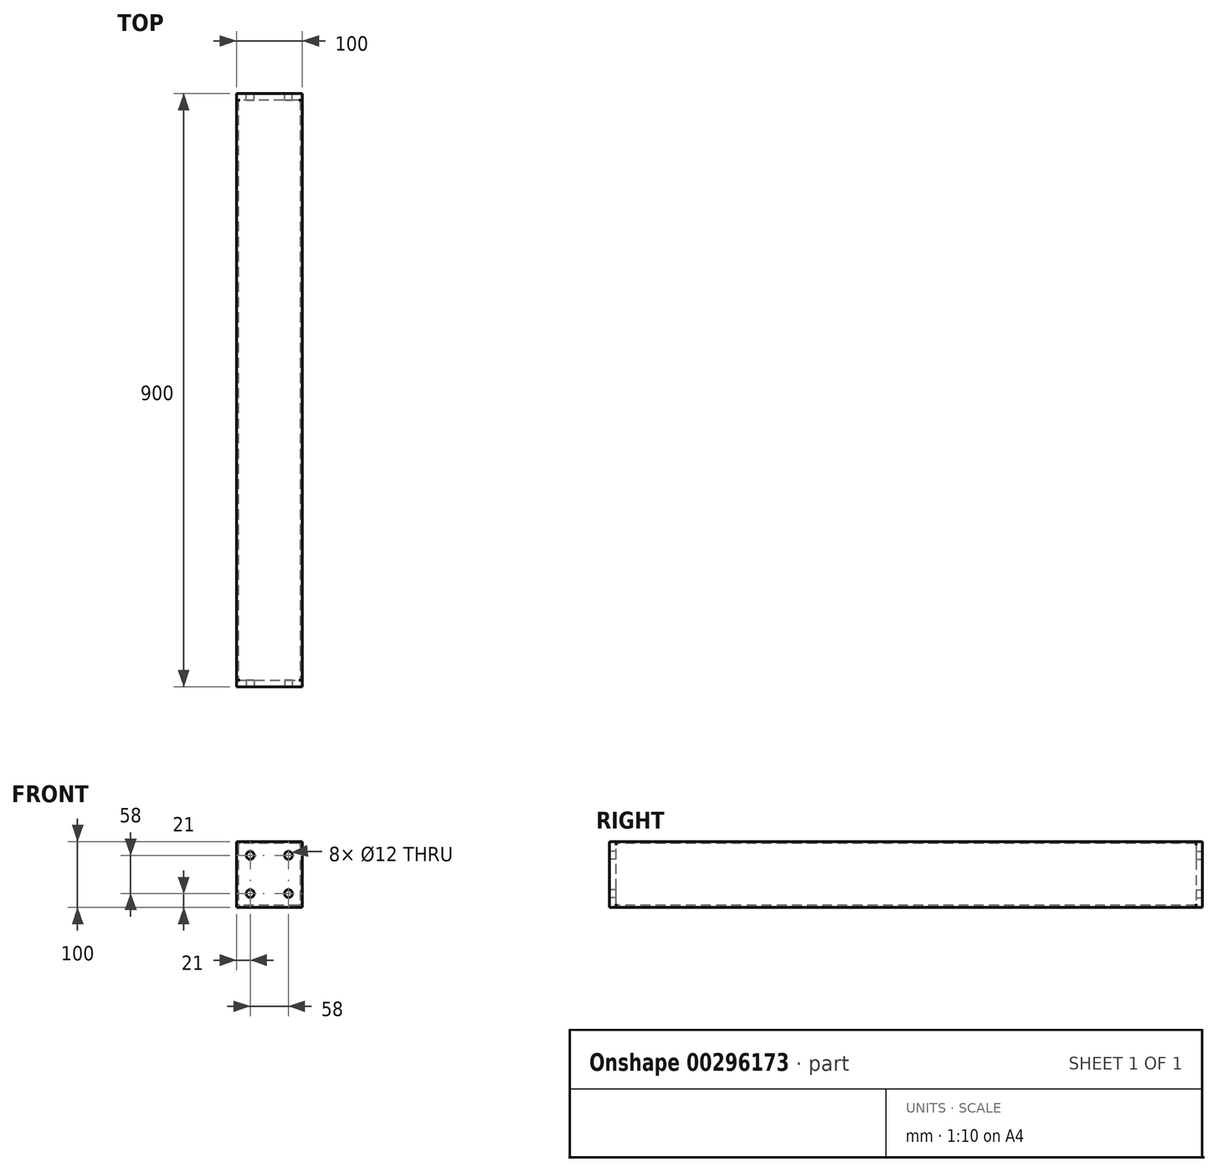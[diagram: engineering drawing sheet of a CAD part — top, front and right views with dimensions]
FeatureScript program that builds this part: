
annotation { "Feature Type Name" : "Feature", "Feature Type Description" : "" }
export const myFeature = defineFeature(function(context is Context, id is Id, definition is map)
    precondition{}
    {
        {
            var Q0;
            Q0=qCreatedBy(makeId("Front.planeOp"),FACE);
            var sketch = newSketch(context, id + "F0", { "sketchPlane" : qUnion([Q0])});
            skLineSegment(sketch, "E0.bottom", {"start": v(45, 50) * mm, "end": v(-45, 50) * mm});
            skLineSegment(sketch, "E0.top", {"start": v(45, -50) * mm, "end": v(-45, -50) * mm});
            skLineSegment(sketch, "E0.left", {"start": v(50, 45) * mm, "end": v(50, -45) * mm});
            skLineSegment(sketch, "E0.right", {"start": v(-50, 45) * mm, "end": v(-50, -45) * mm});
            skPoint(sketch, "E0.middle", {"position": v(0, 0) * mm});
            skPoint(sketch, "E1.visualSharp", {"position": v(-50, 50) * mm});
            skArc(sketch, "E1.filletArc", {"start": v(-45, 50) * mm, "mid": v(-48.54, 48.54) * mm, "end": v(-50, 45) * mm});
            skPoint(sketch, "E2.visualSharp", {"position": v(50, 50) * mm});
            skArc(sketch, "E2.filletArc", {"start": v(50, 45) * mm, "mid": v(48.54, 48.54) * mm, "end": v(45, 50) * mm});
            skPoint(sketch, "E3.visualSharp", {"position": v(50, -50) * mm});
            skArc(sketch, "E3.filletArc", {"start": v(45, -50) * mm, "mid": v(48.54, -48.54) * mm, "end": v(50, -45) * mm});
            skPoint(sketch, "E4.visualSharp", {"position": v(-50, -50) * mm});
            skArc(sketch, "E4.filletArc", {"start": v(-50, -45) * mm, "mid": v(-48.54, -48.54) * mm, "end": v(-45, -50) * mm});
            skArc(sketch, "E5.0", {"start": v(-45, 47) * mm, "mid": v(-46.41, 46.41) * mm, "end": v(-47, 45) * mm});
            skLineSegment(sketch, "E5.1", {"start": v(45, 47) * mm, "end": v(-45, 47) * mm});
            skLineSegment(sketch, "E5.2", {"start": v(-47, 45) * mm, "end": v(-47, -45) * mm});
            skArc(sketch, "E5.3", {"start": v(47, 45) * mm, "mid": v(46.41, 46.41) * mm, "end": v(45, 47) * mm});
            skArc(sketch, "E5.4", {"start": v(-47, -45) * mm, "mid": v(-46.41, -46.41) * mm, "end": v(-45, -47) * mm});
            skLineSegment(sketch, "E5.5", {"start": v(45, -47) * mm, "end": v(-45, -47) * mm});
            skArc(sketch, "E5.6", {"start": v(45, -47) * mm, "mid": v(46.41, -46.41) * mm, "end": v(47, -45) * mm});
            skLineSegment(sketch, "E5.7", {"start": v(47, 45) * mm, "end": v(47, -45) * mm});
            skLineSegment(sketch, "E6.bottom", {"start": v(-45, -45) * mm, "end": v(45, -45) * mm});
            skLineSegment(sketch, "E6.top", {"start": v(-45, 45) * mm, "end": v(45, 45) * mm});
            skLineSegment(sketch, "E6.left", {"start": v(-45, -45) * mm, "end": v(-45, 45) * mm});
            skLineSegment(sketch, "E6.right", {"start": v(45, -45) * mm, "end": v(45, 45) * mm});
            skLineSegment(sketch, "E7", {"start": v(45, 45) * mm, "end": v(-45, -45) * mm, "construction": true});
            skLineSegment(sketch, "E8", {"start": v(-45, 45) * mm, "end": v(45, -45) * mm, "construction": true});
            skLineSegment(sketch, "E9", {"start": v(45, -29) * mm, "end": v(-45, -29) * mm, "construction": true});
            skCircle(sketch, "E10", {"center": v(-29, -29) * mm, "radius": 6 * mm});
            skCircle(sketch, "E11", {"center": v(29, -29) * mm, "radius": 6 * mm});
            skLineSegment(sketch, "E12", {"start": v(29, -29) * mm, "end": v(29, 29) * mm, "construction": true});
            skLineSegment(sketch, "E13", {"start": v(29, 29) * mm, "end": v(-29, 29) * mm, "construction": true});
            skCircle(sketch, "E14", {"center": v(-29, 29) * mm, "radius": 6 * mm});
            skCircle(sketch, "E15", {"center": v(29, 29) * mm, "radius": 6 * mm});
            skCircle(sketch, "E16", {"center": v(0, 0) * mm, "radius": 3 * mm});
            skSolve(sketch);
        }
        {
            var Q0;
            Q0=makeQuery(id+"F0.imprint","IMPRINT",FACE,{"disambiguationData":[TD([[makeQuery(id+"F0.imprint","IMPRINT",EDGE,{"derivedFrom":sQuery(id+"F0.wireOp",EDGE,"E0.bottom")}),1.0]])]});
            extrude(context, id + "F1", {"entities" : qUnion([Q0]), "oppositeDirection" : true, "depth" : (800 + 100) * mm});
        }
        {
            var Q0;
            Q0=makeQuery(id+"F1.opExtrude","CAP_FACE",FACE,{"disambiguationData":[OSD([sQuery(id+"F0.wireOp",EDGE,"E0.bottom"),sQuery(id+"F0.wireOp",EDGE,"E0.top"),sQuery(id+"F0.wireOp",EDGE,"E0.left"),sQuery(id+"F0.wireOp",EDGE,"E0.right"),sQuery(id+"F0.wireOp",EDGE,"E1.filletArc"),sQuery(id+"F0.wireOp",EDGE,"E2.filletArc"),sQuery(id+"F0.wireOp",EDGE,"E3.filletArc"),sQuery(id+"F0.wireOp",EDGE,"E4.filletArc"),sQuery(id+"F0.wireOp",EDGE,"E5.0"),sQuery(id+"F0.wireOp",EDGE,"E5.1"),sQuery(id+"F0.wireOp",EDGE,"E5.2"),sQuery(id+"F0.wireOp",EDGE,"E5.3"),sQuery(id+"F0.wireOp",EDGE,"E5.4"),sQuery(id+"F0.wireOp",EDGE,"E5.5"),sQuery(id+"F0.wireOp",EDGE,"E5.6"),sQuery(id+"F0.wireOp",EDGE,"E5.7")])],"isStart":true});
            cPlane(context, id + "F2", {"entities" : qUnion([Q0]), "cplaneType" : CPlaneType.OFFSET, "offset" : 0 * mm, "width" : 150 * mm, "height" : 150 * mm});
        }
        {
            var Q0;
            Q0=qCreatedBy(id+"F2.planeOp",FACE);
            var sketch = newSketch(context, id + "F3", { "sketchPlane" : qUnion([Q0])});
            skLineSegment(sketch, "E17.bottom", {"start": v(-50, 50) * mm, "end": v(50, 50) * mm});
            skLineSegment(sketch, "E17.top", {"start": v(-50, -50) * mm, "end": v(50, -50) * mm});
            skLineSegment(sketch, "E17.left", {"start": v(-50, 50) * mm, "end": v(-50, -50) * mm});
            skLineSegment(sketch, "E17.right", {"start": v(50, 50) * mm, "end": v(50, -50) * mm});
            skPoint(sketch, "E17.middle", {"position": v(0, 0) * mm});
            skSolve(sketch);
        }
        {
            var Q0;
            Q0=makeQuery(id+"F3.imprint","IMPRINT",FACE,{"disambiguationData":[TD([[makeQuery(id+"F3.imprint","IMPRINT",EDGE,{"derivedFrom":sQuery(id+"F3.wireOp",EDGE,"E17.bottom")}),-1.0]])]});
            extrude(context, id + "F4", {"entities" : qUnion([Q0]), "operationType" : NewBodyOperationType.ADD, "oppositeDirection" : true, "depth" : 10 * mm});
        }
        {
            var Q0;
            Q0=makeQuery(id+"F1.opExtrude","CAP_FACE",FACE,{"disambiguationData":[OSD([sQuery(id+"F0.wireOp",EDGE,"E0.bottom"),sQuery(id+"F0.wireOp",EDGE,"E0.top"),sQuery(id+"F0.wireOp",EDGE,"E0.left"),sQuery(id+"F0.wireOp",EDGE,"E0.right"),sQuery(id+"F0.wireOp",EDGE,"E1.filletArc"),sQuery(id+"F0.wireOp",EDGE,"E2.filletArc"),sQuery(id+"F0.wireOp",EDGE,"E3.filletArc"),sQuery(id+"F0.wireOp",EDGE,"E4.filletArc"),sQuery(id+"F0.wireOp",EDGE,"E5.0"),sQuery(id+"F0.wireOp",EDGE,"E5.1"),sQuery(id+"F0.wireOp",EDGE,"E5.2"),sQuery(id+"F0.wireOp",EDGE,"E5.3"),sQuery(id+"F0.wireOp",EDGE,"E5.4"),sQuery(id+"F0.wireOp",EDGE,"E5.5"),sQuery(id+"F0.wireOp",EDGE,"E5.6"),sQuery(id+"F0.wireOp",EDGE,"E5.7")])],"isStart":false});
            cPlane(context, id + "F5", {"entities" : qUnion([Q0]), "cplaneType" : CPlaneType.OFFSET, "offset" : 0 * mm, "width" : 150 * mm, "height" : 150 * mm});
        }
        {
            var Q0;
            Q0=qCreatedBy(id+"F5.planeOp",FACE);
            var sketch = newSketch(context, id + "F6", { "sketchPlane" : qUnion([Q0])});
            skLineSegment(sketch, "E18.bottom", {"start": v(50, -50) * mm, "end": v(-50, -50) * mm});
            skLineSegment(sketch, "E18.top", {"start": v(50, 50) * mm, "end": v(-50, 50) * mm});
            skLineSegment(sketch, "E18.left", {"start": v(50, -50) * mm, "end": v(50, 50) * mm});
            skLineSegment(sketch, "E18.right", {"start": v(-50, -50) * mm, "end": v(-50, 50) * mm});
            skPoint(sketch, "E18.middle", {"position": v(0, 0) * mm});
            skSolve(sketch);
        }
        {
            var Q0;
            Q0=makeQuery(id+"F6.imprint","IMPRINT",FACE,{"disambiguationData":[TD([[makeQuery(id+"F6.imprint","IMPRINT",EDGE,{"derivedFrom":sQuery(id+"F6.wireOp",EDGE,"E18.bottom")}),-1.0]])]});
            extrude(context, id + "F7", {"entities" : qUnion([Q0]), "operationType" : NewBodyOperationType.ADD, "oppositeDirection" : true, "depth" : 10 * mm});
        }
        {
            var Q0;
            Q0=makeQuery(id+"F4.boolean.opBoolean","MERGE",FACE,{"derivedFrom":[makeQuery(id+"F1.opExtrude","CAP_FACE",FACE,{"disambiguationData":[OSD([sQuery(id+"F0.wireOp",EDGE,"E0.bottom"),sQuery(id+"F0.wireOp",EDGE,"E0.top"),sQuery(id+"F0.wireOp",EDGE,"E0.left"),sQuery(id+"F0.wireOp",EDGE,"E0.right"),sQuery(id+"F0.wireOp",EDGE,"E1.filletArc"),sQuery(id+"F0.wireOp",EDGE,"E2.filletArc"),sQuery(id+"F0.wireOp",EDGE,"E3.filletArc"),sQuery(id+"F0.wireOp",EDGE,"E4.filletArc"),sQuery(id+"F0.wireOp",EDGE,"E5.0"),sQuery(id+"F0.wireOp",EDGE,"E5.1"),sQuery(id+"F0.wireOp",EDGE,"E5.2"),sQuery(id+"F0.wireOp",EDGE,"E5.3"),sQuery(id+"F0.wireOp",EDGE,"E5.4"),sQuery(id+"F0.wireOp",EDGE,"E5.5"),sQuery(id+"F0.wireOp",EDGE,"E5.6"),sQuery(id+"F0.wireOp",EDGE,"E5.7")])],"isStart":true}),makeQuery(id+"F4.opExtrude","CAP_FACE",FACE,{"disambiguationData":[OSD([sQuery(id+"F3.wireOp",EDGE,"E17.bottom"),sQuery(id+"F3.wireOp",EDGE,"E17.top"),sQuery(id+"F3.wireOp",EDGE,"E17.left"),sQuery(id+"F3.wireOp",EDGE,"E17.right")])],"isStart":true})]});
            var sketch = newSketch(context, id + "F8", { "sketchPlane" : qUnion([Q0])});
            skLineSegment(sketch, "E19.bottom", {"start": v(-45, -45) * mm, "end": v(45, -45) * mm});
            skLineSegment(sketch, "E19.top", {"start": v(-45, 45) * mm, "end": v(45, 45) * mm});
            skLineSegment(sketch, "E19.left", {"start": v(-45, -45) * mm, "end": v(-45, 45) * mm});
            skLineSegment(sketch, "E19.right", {"start": v(45, -45) * mm, "end": v(45, 45) * mm});
            skPoint(sketch, "E19.middle", {"position": v(0, 0) * mm});
            skLineSegment(sketch, "E20", {"start": v(45, 45) * mm, "end": v(-45, -45) * mm, "construction": true});
            skLineSegment(sketch, "E21", {"start": v(-45, 45) * mm, "end": v(45, -45) * mm, "construction": true});
            skLineSegment(sketch, "E22", {"start": v(45, -29) * mm, "end": v(-45, -29) * mm, "construction": true});
            skCircle(sketch, "E23", {"center": v(-29, -29) * mm, "radius": 6 * mm});
            skCircle(sketch, "E24", {"center": v(29, -29) * mm, "radius": 6 * mm});
            skLineSegment(sketch, "E25", {"start": v(29, -29) * mm, "end": v(29, 29) * mm, "construction": true});
            skLineSegment(sketch, "E26", {"start": v(29, 29) * mm, "end": v(-29, 29) * mm, "construction": true});
            skCircle(sketch, "E27", {"center": v(-29, 29) * mm, "radius": 6 * mm});
            skCircle(sketch, "E28", {"center": v(29, 29) * mm, "radius": 6 * mm});
            skCircle(sketch, "E29", {"center": v(0, 0) * mm, "radius": 3 * mm});
            skSolve(sketch);
        }
        {
            var Q0;
            Q0=makeQuery(id+"F8.imprint","IMPRINT",FACE,{"disambiguationData":[TD([[makeQuery(id+"F8.imprint","IMPRINT",EDGE,{"derivedFrom":sQuery(id+"F8.wireOp",EDGE,"E27")}),1.0]])]});
            var Q1;
            Q1=makeQuery(id+"F8.imprint","IMPRINT",FACE,{"disambiguationData":[TD([[makeQuery(id+"F8.imprint","IMPRINT",EDGE,{"derivedFrom":sQuery(id+"F8.wireOp",EDGE,"E28")}),1.0]])]});
            var Q2;
            Q2=makeQuery(id+"F8.imprint","IMPRINT",FACE,{"disambiguationData":[TD([[makeQuery(id+"F8.imprint","IMPRINT",EDGE,{"derivedFrom":sQuery(id+"F8.wireOp",EDGE,"E24")}),1.0]])]});
            var Q3;
            Q3=makeQuery(id+"F8.imprint","IMPRINT",FACE,{"disambiguationData":[TD([[makeQuery(id+"F8.imprint","IMPRINT",EDGE,{"derivedFrom":sQuery(id+"F8.wireOp",EDGE,"E23")}),1.0]])]});
            extrude(context, id + "F9", {"entities" : qUnion([Q0, Q1, Q2, Q3]), "operationType" : NewBodyOperationType.REMOVE, "endBound" : BoundingType.UP_TO_NEXT, "oppositeDirection" : true, "depth" : 25 * mm});
        }
        {
            var Q0;
            Q0=makeQuery(id+"F7.boolean.opBoolean","MERGE",FACE,{"derivedFrom":[makeQuery(id+"F1.opExtrude","CAP_FACE",FACE,{"disambiguationData":[OSD([sQuery(id+"F0.wireOp",EDGE,"E0.bottom"),sQuery(id+"F0.wireOp",EDGE,"E0.top"),sQuery(id+"F0.wireOp",EDGE,"E0.left"),sQuery(id+"F0.wireOp",EDGE,"E0.right"),sQuery(id+"F0.wireOp",EDGE,"E1.filletArc"),sQuery(id+"F0.wireOp",EDGE,"E2.filletArc"),sQuery(id+"F0.wireOp",EDGE,"E3.filletArc"),sQuery(id+"F0.wireOp",EDGE,"E4.filletArc"),sQuery(id+"F0.wireOp",EDGE,"E5.0"),sQuery(id+"F0.wireOp",EDGE,"E5.1"),sQuery(id+"F0.wireOp",EDGE,"E5.2"),sQuery(id+"F0.wireOp",EDGE,"E5.3"),sQuery(id+"F0.wireOp",EDGE,"E5.4"),sQuery(id+"F0.wireOp",EDGE,"E5.5"),sQuery(id+"F0.wireOp",EDGE,"E5.6"),sQuery(id+"F0.wireOp",EDGE,"E5.7")])],"isStart":false}),makeQuery(id+"F7.opExtrude","CAP_FACE",FACE,{"disambiguationData":[OSD([sQuery(id+"F6.wireOp",EDGE,"E18.bottom"),sQuery(id+"F6.wireOp",EDGE,"E18.top"),sQuery(id+"F6.wireOp",EDGE,"E18.left"),sQuery(id+"F6.wireOp",EDGE,"E18.right")])],"isStart":true})]});
            var sketch = newSketch(context, id + "F10", { "sketchPlane" : qUnion([Q0])});
            skLineSegment(sketch, "E30.bottom", {"start": v(-45, -45) * mm, "end": v(45, -45) * mm});
            skLineSegment(sketch, "E30.top", {"start": v(-45, 45) * mm, "end": v(45, 45) * mm});
            skLineSegment(sketch, "E30.left", {"start": v(-45, -45) * mm, "end": v(-45, 45) * mm});
            skLineSegment(sketch, "E30.right", {"start": v(45, -45) * mm, "end": v(45, 45) * mm});
            skPoint(sketch, "E30.middle", {"position": v(0, 0) * mm});
            skLineSegment(sketch, "E31", {"start": v(45, 45) * mm, "end": v(-45, -45) * mm, "construction": true});
            skLineSegment(sketch, "E32", {"start": v(-45, 45) * mm, "end": v(45, -45) * mm, "construction": true});
            skLineSegment(sketch, "E33", {"start": v(45, -29) * mm, "end": v(-45, -29) * mm, "construction": true});
            skCircle(sketch, "E34", {"center": v(-29, -29) * mm, "radius": 6 * mm});
            skCircle(sketch, "E35", {"center": v(29, -29) * mm, "radius": 6 * mm});
            skLineSegment(sketch, "E36", {"start": v(29, -29) * mm, "end": v(29, 29) * mm, "construction": true});
            skLineSegment(sketch, "E37", {"start": v(29, 29) * mm, "end": v(-29, 29) * mm, "construction": true});
            skCircle(sketch, "E38", {"center": v(-29, 29) * mm, "radius": 6 * mm});
            skCircle(sketch, "E39", {"center": v(29, 29) * mm, "radius": 6 * mm});
            skCircle(sketch, "E40", {"center": v(0, 0) * mm, "radius": 3 * mm});
            skSolve(sketch);
        }
        {
            var Q0;
            Q0=makeQuery(id+"F10.imprint","IMPRINT",FACE,{"disambiguationData":[TD([[makeQuery(id+"F10.imprint","IMPRINT",EDGE,{"derivedFrom":sQuery(id+"F10.wireOp",EDGE,"E38")}),1.0]])]});
            var Q1;
            Q1=makeQuery(id+"F10.imprint","IMPRINT",FACE,{"disambiguationData":[TD([[makeQuery(id+"F10.imprint","IMPRINT",EDGE,{"derivedFrom":sQuery(id+"F10.wireOp",EDGE,"E39")}),1.0]])]});
            var Q2;
            Q2=makeQuery(id+"F10.imprint","IMPRINT",FACE,{"disambiguationData":[TD([[makeQuery(id+"F10.imprint","IMPRINT",EDGE,{"derivedFrom":sQuery(id+"F10.wireOp",EDGE,"E35")}),1.0]])]});
            var Q3;
            Q3=makeQuery(id+"F10.imprint","IMPRINT",FACE,{"disambiguationData":[TD([[makeQuery(id+"F10.imprint","IMPRINT",EDGE,{"derivedFrom":sQuery(id+"F10.wireOp",EDGE,"E34")}),1.0]])]});
            extrude(context, id + "F11", {"entities" : qUnion([Q0, Q1, Q2, Q3]), "operationType" : NewBodyOperationType.REMOVE, "endBound" : BoundingType.UP_TO_NEXT, "oppositeDirection" : true, "depth" : 25 * mm});
        }
    });
